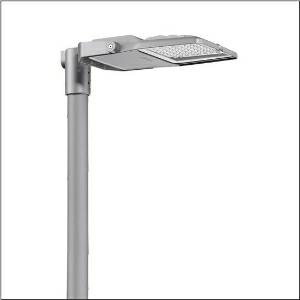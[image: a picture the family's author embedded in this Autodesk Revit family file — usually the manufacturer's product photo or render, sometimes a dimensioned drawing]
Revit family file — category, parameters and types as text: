
# Revit family: floodlight_fl_21_iq_mini___pl64_5xa7772b2e3a_76f3
name_source: partatom
category: Lighting Fixtures
units: mm (PartAtom-declared; Revit-internal decimal feet)

## family parameters
Cut with Voids When Loaded = No
Host = Face
Light Source = No
Part Type = Normal
Room Calculation Point = No
Round Connector Dimension = Use Diameter
Shared = No

## types (1)
- --- (1 x LED, 6020 lm, 45.5 W, 3000K)
    Apparent Load = 46 VA
    CIE Flux Codes = 28 80 98 100 100
    Color Rendering = 70
    Color Temperature = 3000K
    Default Elevation = 1800 mm
    Description = Floodlight FL 21 iQ mini, floodlight, primary light control with lens, of PMMA, primary optical cover: protective disc, of toughened safety glass, transparent, light distribution: PL64, light emission: direct distribution, installation type: surface-mounted, lamps: LED, High Power LED, rated values: 6.020lm | 45,5W | 132,3lm/W (begin service life); end service life: 6.020lm | 48W; at 50% lumin. flux: 3.010lm | 21,5W | 140lm/W, colour temperature: 3000K, colour rendering: CRI > 70, light colour: 730, light setting 1 begin service life: 100% | 6.020lm | 45,5W | 132,3lm/W | 3.000K, light setting 1 end service life: 48W, further light settings possible, control: pre-setting: linear dimming characteristic, Auto-Match, Temp-Guard, Night-Set, Smart-Wire, Desk-Remote (wireless, voltage-free reading and setting of iQ features in the workshop via application-optimized NFC function/RFID function), optimised constant luminous flux control (CLO 2.0), Light-Fading, Lumen-Switch, with terminal, 6-pole, mains connection: 220..240V, AC, 50/60Hz, luminaire housing, of diecast aluminium, powder-coated, SITECO metallic grey (DB 702S), corrosivity category C5 mid according to DIN EN ISO 12944suitable for swimming poolschlorine-resistant, sealing non-destructively replaceable, please order mast flange separately, mast bracket, of steel, galvanised, powder-coated, protection rating (complete): IP66, insulation class (complete): insulation class II (safety insulation), certification: CE, ENEC, VDE, protection symbol: D, impact resistance: IK08, permissible operating ambient temperature: -40..+40°C, permissible operating ambient temperature for outdoor applications: -40..+50°C, standard: DIN EN 12944, LABS conformity tested according to VDMA 24364:2018-05, packaging unit: 1 piece

Light Distribution: PL64
    Height = 70 mm
    Lamp = 1 x LED
    Lamp Light Flux = 6020 lm
    Lamp Power = 45.5 W
    Lamp count = 1
    Length = 485 mm
    Luminous efficacy = 132 lm/W
    Manufacturer = Siteco
    ModVariant = No
    Model = 5XA7772B2E3A
    Number of Poles = 1
    OnlyDefault = Yes
    Power Factor = 1
    Product Name = Floodlight FL 21 iQ mini | PL64
    Product group = floodlight | pylon annexe
    ProductGroupID = 6201
    Protection Class = Protection class II
    Protection Degree = IP 66
    RLX_Detail_Level = 1
    RLX_Emergency_Light_Flux = 0 lm
    RLX_Emergency_Type = 0
    RLX_Emergency_Type_DB = No
    RlxData = <blob elided: 101381 chars, md5=f1608d5f>
    Socket = socket
    Standby Power = 0 W
    System Light Flux = 6020 lm
    System Power = 46 W
    Type Comments = factory setting: luminous flux: 100 % | dim-lin: 254 | 463 mA
    Type Image = l_1007125.jpg
    URL = http://relux.com
    VarID = @adj_166379
    Voltage = 0 V
    Weight = 0.00 kg
    Width = 337 mm

## geometry (parser evidence)
native form markers: Blend x4, Sweep x13
no freeform markers — native parametric forms only
